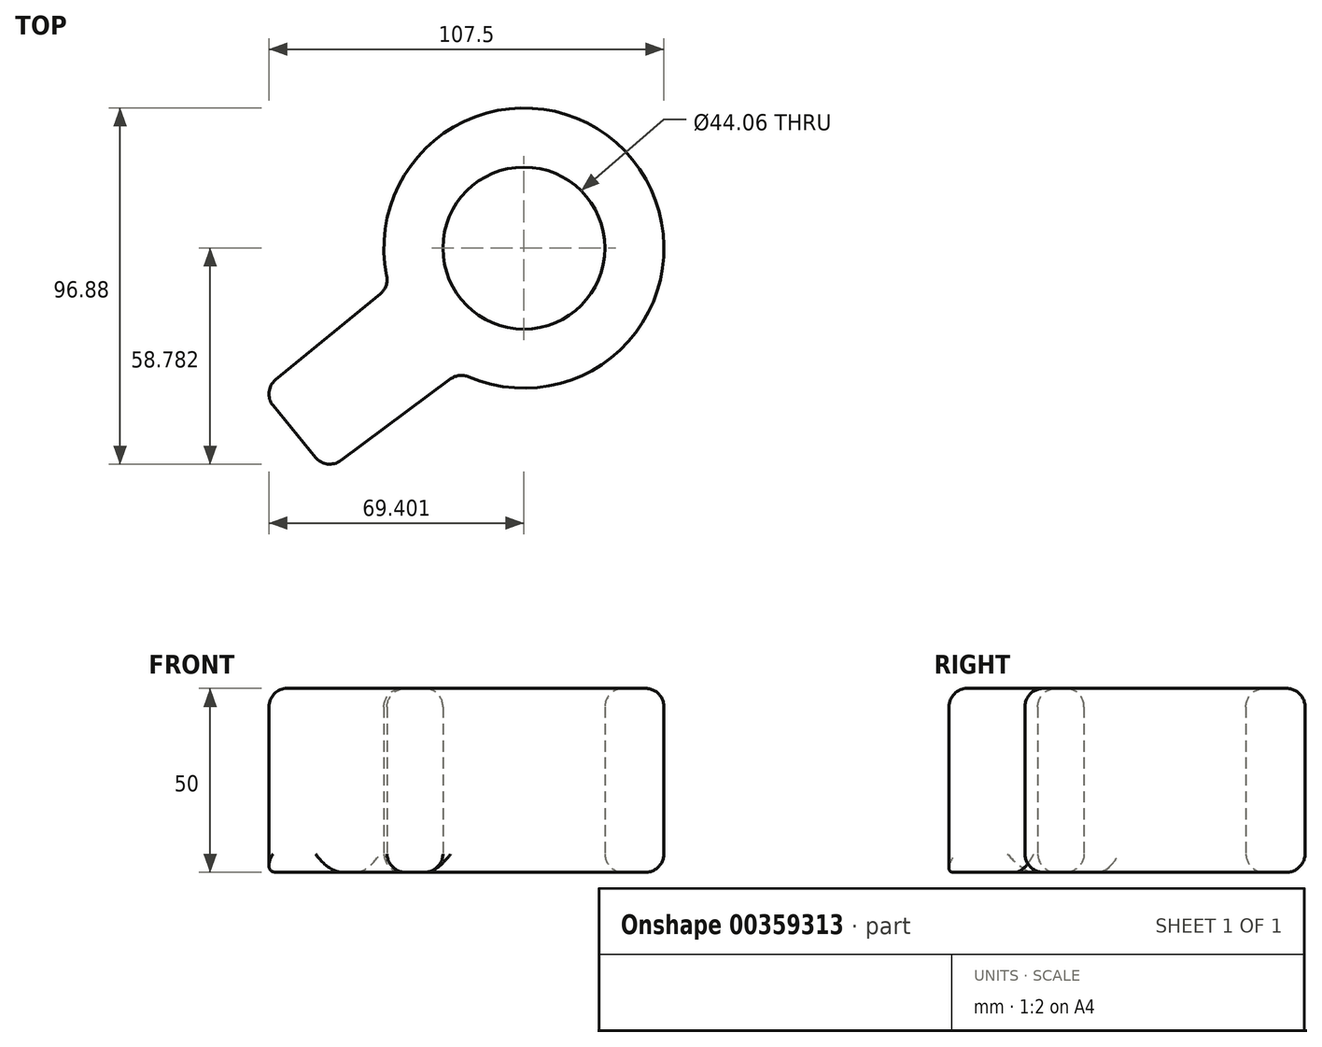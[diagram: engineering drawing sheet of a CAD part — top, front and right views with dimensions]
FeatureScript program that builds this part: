
annotation { "Feature Type Name" : "Feature", "Feature Type Description" : "" }
export const myFeature = defineFeature(function(context is Context, id is Id, definition is map)
    precondition{}
    {
        {
            var Q0;
            Q0=qCreatedBy(makeId("Top.planeOp"),FACE);
            var sketch = newSketch(context, id + "F0", { "sketchPlane" : qUnion([Q0])});
            skCircle(sketch, "E0", {"center": v(36.64, 26.93) * mm, "radius": 38.1 * mm});
            skCircle(sketch, "E1", {"center": v(36.64, 26.93) * mm, "radius": 22.03 * mm});
            skLineSegment(sketch, "E2", {"start": v(0, 16.49) * mm, "end": v(-34.8, -12.05) * mm});
            skLineSegment(sketch, "E3", {"start": v(-34.8, -12.05) * mm, "end": v(-17.04, -33.7) * mm});
            skLineSegment(sketch, "E4", {"start": v(-17.04, -33.7) * mm, "end": v(19.11, -6.9) * mm});
            skSolve(sketch);
        }
        {
            var Q0;
            Q0 = qSketchRegion(id + "F0", true);
            extrude(context, id + "F1", {"entities" : qUnion([Q0]), "depth" : 50 * mm});
        }
        {
            var Q0;
            Q0=makeQuery(id+"F1.opExtrude","CAP_EDGE",EDGE,{"disambiguationData":[OSD([sQuery(id+"F0.wireOp",EDGE,"E0")])],"isStart":false});
            var Q1;
            Q1=makeQuery(id+"F1.opExtrude","CAP_EDGE",EDGE,{"disambiguationData":[OSD([sQuery(id+"F0.wireOp",EDGE,"E1")])],"isStart":false});
            var Q2;
            Q2=makeQuery(id+"F1.opExtrude","CAP_EDGE",EDGE,{"disambiguationData":[OSD([sQuery(id+"F0.wireOp",EDGE,"E2")])],"isStart":false});
            var Q3;
            Q3=makeQuery(id+"F1.opExtrude","CAP_EDGE",EDGE,{"disambiguationData":[OSD([sQuery(id+"F0.wireOp",EDGE,"E4")])],"isStart":false});
            var Q4;
            Q4=makeQuery(id+"F1.opExtrude","SWEPT_EDGE",EDGE,{"disambiguationData":[OSD([sQuery(id+"F0.wireOp",EDGE,"E0"),sQuery(id+"F0.wireOp",EDGE,"E2")])]});
            var Q5;
            Q5=makeQuery(id+"F1.opExtrude","SWEPT_EDGE",EDGE,{"disambiguationData":[OSD([sQuery(id+"F0.wireOp",EDGE,"E2"),sQuery(id+"F0.wireOp",EDGE,"E3")])]});
            var Q6;
            Q6=makeQuery(id+"F1.opExtrude","SWEPT_EDGE",EDGE,{"disambiguationData":[OSD([sQuery(id+"F0.wireOp",EDGE,"E0"),sQuery(id+"F0.wireOp",EDGE,"E4")])]});
            var Q7;
            Q7=makeQuery(id+"F1.opExtrude","SWEPT_EDGE",EDGE,{"disambiguationData":[OSD([sQuery(id+"F0.wireOp",EDGE,"E3"),sQuery(id+"F0.wireOp",EDGE,"E4")])]});
            var Q8;
            Q8=makeQuery(id+"F1.opExtrude","SWEPT_FACE",FACE,{"disambiguationData":[OSD([sQuery(id+"F0.wireOp",EDGE,"E3")])]});
            var Q9;
            Q9=makeQuery(id+"F1.opExtrude","CAP_EDGE",EDGE,{"disambiguationData":[OSD([sQuery(id+"F0.wireOp",EDGE,"E0")])],"isStart":true});
            var Q10;
            Q10=makeQuery(id+"F1.opExtrude","CAP_EDGE",EDGE,{"disambiguationData":[OSD([sQuery(id+"F0.wireOp",EDGE,"E1")])],"isStart":true});
            fillet(context, id + "F2", {"entities" : qUnion([Q0, Q1, Q2, Q3, Q4, Q5, Q6, Q7, Q8, Q9, Q10]), "radius" : 5 * mm, "tangentPropagation" : true, "allowEdgeOverflow" : false});
        }
    });
